# Revit family: HM
name_source: partatom
category: Modelos genéricos
revit_build: Autodesk Revit 2017 (Build: 20160225_1515(x64)
units: mm (PartAtom-declared; Revit-internal decimal feet)

## family parameters
Compartido = No
Corte con vacíos al cargar = No
Cota de conector redondo = Diámetro de uso
Puede alojar armadura = No
Punto de cálculo de habitación = No
Se basa en plano de trabajo = No
Siempre vertical = No
Tipo de pieza = Normal

## types (13) — shared parameters
Emig = 100 mm  [stored 0.328084 ft]
Fabricante = Casals Ventilación
URL = www.casals.com

## per-type parameters (varying)
| type | A | A/2 | B | B/2 | D | D/2 | Dimensiones | E | E ARO | E ENVOL | eForat | i |
| HM 30 | 374 mm  [stored 1.22703 ft] | 187 mm  [stored 0.613517 ft] | 355 mm | 178 mm | 305 mm  [stored 1.00066 ft] | 153 mm | 374x374x350 | 350 mm  [stored 1.14829 ft] | 2 mm  [stored 0.00656168 ft] | 2 mm  [stored 0.00656168 ft] | -2 mm  [stored -0.00656168 ft] | 10 mm  [stored 0.0328084 ft] |
| HM 35 | 434 mm | 217 mm  [stored 0.711942 ft] | 395 mm  [stored 1.29593 ft] | 198 mm | 365 mm  [stored 1.19751 ft] | 183 mm | 434x434x350 | 350 mm  [stored 1.14829 ft] | 2 mm  [stored 0.00656168 ft] | 2 mm  [stored 0.00656168 ft] | -2 mm  [stored -0.00656168 ft] | 10 mm  [stored 0.0328084 ft] |
| HM 40 | 472 mm | 236 mm | 450 mm | 225 mm  [stored 0.738189 ft] | 403 mm | 202 mm | 472x472x440 | 440 mm | 2 mm  [stored 0.00656168 ft] | 2 mm  [stored 0.00656168 ft] | -2 mm  [stored -0.00656168 ft] | 10 mm  [stored 0.0328084 ft] |
| HM 45 | 525 mm | 263 mm | 500 mm | 250 mm  [stored 0.82021 ft] | 452 mm | 226 mm  [stored 0.74147 ft] | 525x525x455 | 455 mm | 2 mm  [stored 0.00656168 ft] | 2 mm  [stored 0.00656168 ft] | -2 mm  [stored -0.00656168 ft] | 12 mm  [stored 0.0393701 ft] |
| HM 50 | 600 mm | 300 mm | 560 mm | 280 mm  [stored 0.918635 ft] | 504 mm | 252 mm  [stored 0.826772 ft] | 600x600x440 | 440 mm | 2 mm  [stored 0.00656168 ft] | 2 mm  [stored 0.00656168 ft] | -2 mm  [stored -0.00656168 ft] | 12 mm  [stored 0.0393701 ft] |
| HM 56 | 646 mm | 323 mm  [stored 1.05971 ft] | 620 mm | 310 mm  [stored 1.01706 ft] | 559 mm | 280 mm  [stored 0.918635 ft] | 646x646x560 | 560 mm | 2 mm  [stored 0.00656168 ft] | 2 mm  [stored 0.00656168 ft] | -2 mm  [stored -0.00656168 ft] | 12 mm  [stored 0.0393701 ft] |
| HM 63 | 725 mm | 363 mm | 690 mm | 345 mm  [stored 1.13189 ft] | 633 mm | 317 mm | 725x725x550 | 550 mm | 2 mm  [stored 0.00656168 ft] | 2 mm  [stored 0.00656168 ft] | -2 mm  [stored -0.00656168 ft] | 12 mm  [stored 0.0393701 ft] |
| HM 71 | 802 mm | 401 mm | 770 mm | 385 mm  [stored 1.26312 ft] | 715 mm | 358 mm | 802x802x600 | 600 mm | 2 mm  [stored 0.00656168 ft] | 2 mm  [stored 0.00656168 ft] | -2 mm  [stored -0.00656168 ft] | 12 mm  [stored 0.0393701 ft] |
| HM 80 | 892 mm | 446 mm | 860 mm | 430 mm | 801 mm | 401 mm | 892x892x600 | 600 mm | 2 mm  [stored 0.00656168 ft] | 2 mm  [stored 0.00656168 ft] | -2 mm  [stored -0.00656168 ft] | 12 mm  [stored 0.0393701 ft] |
| HM 90 | 1000 mm | 500 mm | 970 mm | 485 mm | 904 mm | 452 mm | 1000x1000x820 | 820 mm | 3 mm  [stored 0.00984252 ft] | 3 mm  [stored 0.00984252 ft] | -3 mm  [stored -0.00984252 ft] | 12 mm  [stored 0.0393701 ft] |
| HM 100 | 1115 mm | 558 mm | 1070 mm | 535 mm | 1013 mm | 507 mm | 1115x1115x820 | 820 mm | 3 mm  [stored 0.00984252 ft] | 3 mm  [stored 0.00984252 ft] | -3 mm  [stored -0.00984252 ft] | 12 mm  [stored 0.0393701 ft] |
| HM 112 | 1234 mm | 617 mm | 1190 mm | 595 mm | 1132 mm | 566 mm | 1234x1234x1000 | 1000 mm | 5 mm  [stored 0.0164042 ft] | 3 mm  [stored 0.00984252 ft] | -5 mm  [stored -0.0164042 ft] | 12 mm  [stored 0.0393701 ft] |
| HM 125 | 1365 mm | 683 mm | 1320 mm | 660 mm | 1263 mm | 632 mm | 1365x1365x1000 | 1000 mm | 6 mm  [stored 0.019685 ft] | 3 mm  [stored 0.00984252 ft] | -6 mm  [stored -0.019685 ft] | 15 mm  [stored 0.0492126 ft] |

note: [stored X ft] marks values corroborated as IEEE doubles in the binary element streams (Revit-internal decimal feet)
